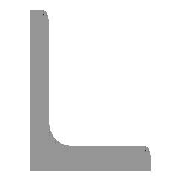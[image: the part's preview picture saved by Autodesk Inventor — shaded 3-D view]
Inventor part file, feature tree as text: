
AUTODESK INVENTOR PART (.ipt)
format: ipt  version: 2022 (Build 260153000, 153)  size: 162,816 bytes
history: native  units: mm (DEFAULTED — no unit token found)
features: other x5, sketch x2, sweep x1, plane x1
ambient origin geometry x8: Origin, YZ Plane, XZ Plane, XY Plane, X Axis, Y Axis, Z Axis, Center Point
bodies: Solid1 (feature_tree), Body (feature_tree)
feature tree (9):
  parser-record x1  (decoder bookkeeping rows leaked as tree rows — omitted from the tree; the rows remain in map.json)
  other  "Driven Length"
  other  "Start plane"
  other  "End plane"
  sweep  "Sweep Path"
  other  "Orientation Work Plane"
  sketch  "Sketch3"  dims[d3=50.0mm d4=30.0mm]
  plane  "Work Plane10"
  sketch  "Sketch4"  dims[d5=50.0mm d6=30.0mm d7=4.0mm d8=4.0mm d9=4.0mm d10=4.0mm d17=5.0mm d18=2.5mm d19=8.8mm d20=8.8mm d21=-0.0mm d22=2815.406592mm d23=90.0deg d24=2815.406592mm d25=0.0mm d26=0.0mm]
